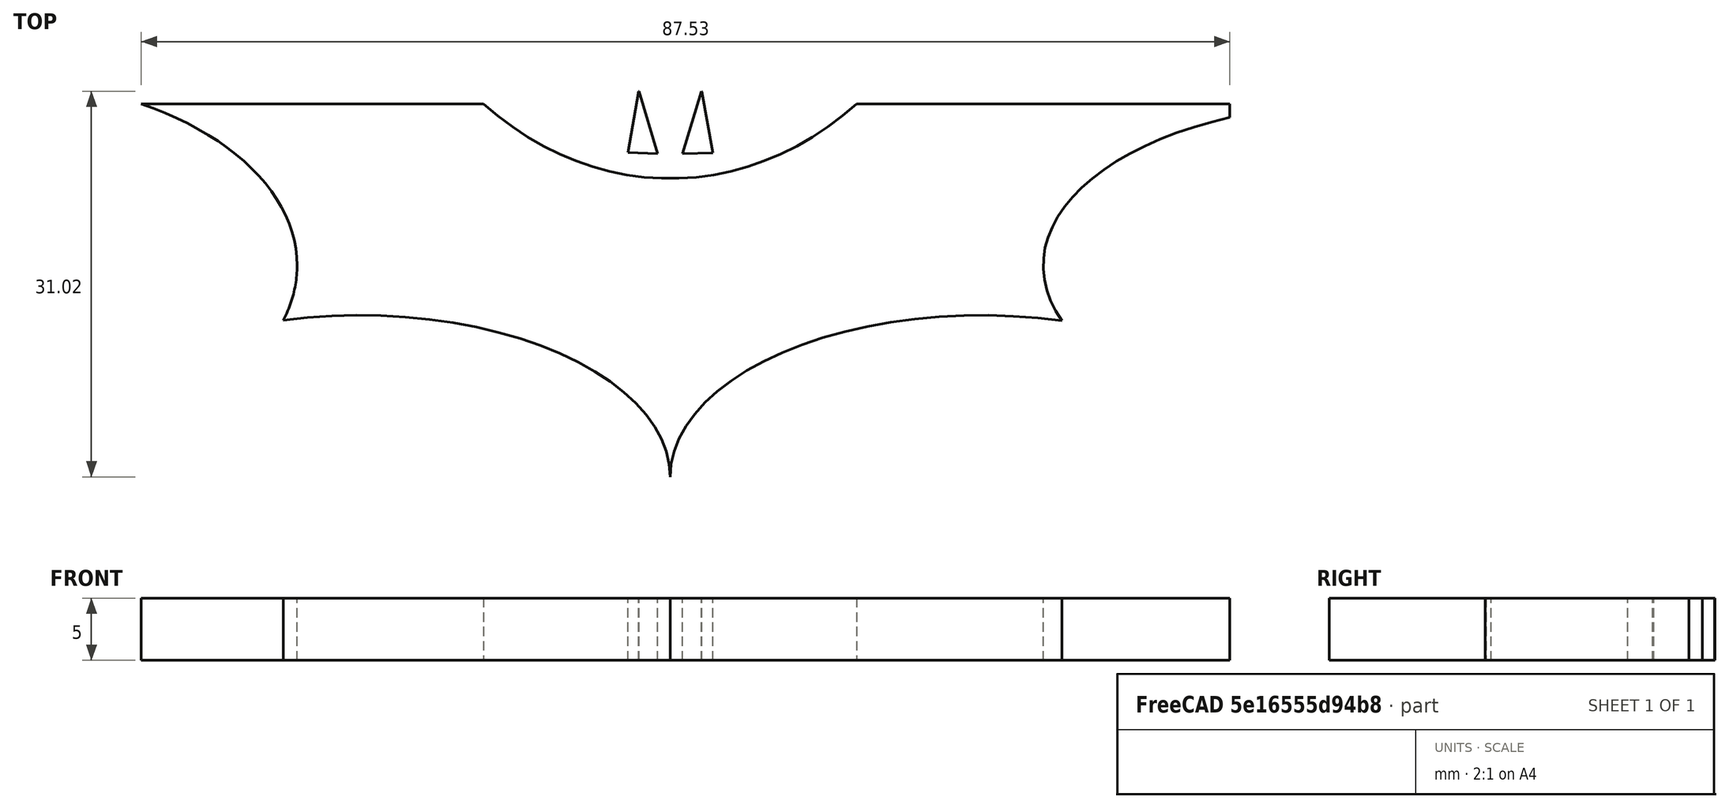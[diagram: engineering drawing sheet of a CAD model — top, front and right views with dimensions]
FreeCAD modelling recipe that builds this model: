
FCSTD DOCUMENT  (FreeCAD 0.16R6706 (Git))
Label: Batman Logo
License: All rights reserved
LicenseURL: http://en.wikipedia.org/wiki/All_rights_reserved
objects: Part::Feature×11, Part::Extrusion×7, Part::Cut×5, Part::Line×5, Part::Box×1
note: 29 computed .brp shape members not serialized (recipe doc carries the construction recipe); baked Part::Feature solids carry a one-line shape summary decoded from their .brp

FEATURE [Part::Box] Box  label="Cubo"
  Height = 5
  Length = 90
  Width = 30
FEATURE [Part::Feature] Face
  shape: bbox 71 x 28.35 x 2e-07 mm, 1 faces, 0 solids (baked)
FEATURE [Part::Extrusion] Extrude  label="Elipse Abajo 1"
  Base = -> Face
  Dir = (0,0,5)
  Placement = pos=(20,0,0) rot=(0,0,1;0rad)
  Solid = false
FEATURE [Part::Feature] Face001
  shape: bbox 71 x 28.35 x 2e-07 mm, 1 faces, 0 solids (baked)
FEATURE [Part::Extrusion] Extrude001  label="Elipse Abajo 2"
  Base = -> Face001
  Dir = (0,0,5)
  Placement = pos=(70,0,0) rot=(0,0,1;0rad)
  Solid = false
FEATURE [Part::Feature] Face002
  shape: bbox 71.47 x 32.68 x 2e-07 mm, 1 faces, 0 solids (baked)
FEATURE [Part::Extrusion] Extrude002  label="Elipse Lado Izq"
  Base = -> Face002
  Dir = (0,0,5)
  Placement = pos=(-10,17,0) rot=(0,0,1;0rad)
  Solid = false
FEATURE [Part::Feature] Face003
  shape: bbox 71 x 28.35 x 2e-07 mm, 1 faces, 0 solids (baked)
FEATURE [Part::Extrusion] Extrude003
  Base = -> Face003
  Dir = (0,0,5)
  Placement = pos=(100,17,0) rot=(0,0,1;0rad)
  Solid = false
FEATURE [Part::Cut] Cut
  Base = -> Box
  Tool = -> Extrude002
FEATURE [Part::Cut] Cut001
  Base = -> Cut
  Tool = -> Extrude
FEATURE [Part::Cut] Cut002
  Base = -> Cut001
  Tool = -> Extrude003
FEATURE [Part::Cut] Cut003
  Base = -> Cut002
  Tool = -> Extrude001
FEATURE [Part::Feature] Face004
  Placement = pos=(0,3,0) rot=(0,0,1;0rad)
  shape: bbox 54.52 x 88.54 x 2e-07 mm, 1 faces, 0 solids (baked)
FEATURE [Part::Extrusion] Extrude004
  Base = -> Face004
  Dir = (0,0,5)
  Placement = pos=(0,1,0) rot=(0,0,1;0rad)
  Solid = false
FEATURE [Part::Cut] Cut004  label="Base"
  Base = -> Cut003
  Tool = -> Extrude004
FEATURE [Part::Line] Line  label="Línea"
  Placement = pos=(-0.9,0.1,0) rot=(0,0,-1;0.174533rad)
  X1 = 0
  X2 = 0
  Y1 = 0
  Y2 = 5
  Z1 = 0
  Z2 = 0
FEATURE [Part::Line] Line003  label="Línea003"
  X1 = 0
  X2 = 1.5
  Y1 = 5
  Y2 = 0
  Z1 = 0
  Z2 = 0
FEATURE [Part::Line] Line004  label="Línea004"
  X1 = 1.5
  X2 = 3.5
  Y1 = 0
  Y2 = 0
  Z1 = 0
  Z2 = 0
FEATURE [Part::Line] Line005  label="Línea005"
  X1 = 3.5
  X2 = 5
  Y1 = 0
  Y2 = 5
  Z1 = 0
  Z2 = 0
FEATURE [Part::Line] Line006  label="Línea006"
  Placement = pos=(1,-0.8,0) rot=(0,0,1;0.174533rad)
  X1 = 5
  X2 = 5
  Y1 = 5
  Y2 = 0
  Z1 = 0
  Z2 = 0
FEATURE [Part::Feature] Edge
  shape: bbox 0.03176 x 0.02404 x 2e-07 mm, 0 faces, 0 solids (baked)
FEATURE [Part::Feature] Edge001
  shape: bbox 2.4 x 0.1 x 2e-07 mm, 0 faces, 0 solids (baked)
FEATURE [Part::Feature] Edge002
  shape: bbox 2.424 x 0.06824 x 2e-07 mm, 0 faces, 0 solids (baked)
FEATURE [Part::Feature] Edge003
  shape: bbox 0.0558 x 0.007721 x 2e-07 mm, 0 faces, 0 solids (baked)
FEATURE [Part::Feature] Face005
  Placement = pos=(42.5,26,0) rot=(0,0,1;0rad)
  shape: bbox 3.053 x 5.783 x 2e-07 mm, 1 faces, 0 solids (baked)
FEATURE [Part::Feature] Face006
  Placement = pos=(42.5,26,0) rot=(0,0,1;0rad)
  shape: bbox 3.034 x 5.814 x 2e-07 mm, 1 faces, 0 solids (baked)
FEATURE [Part::Extrusion] Extrude005
  Base = -> Face006
  Dir = (0,0,5)
  Solid = false
FEATURE [Part::Extrusion] Extrude006
  Base = -> Face005
  Dir = (0,0,5)
  Solid = false
